# Revit family: Lollygagger Lounge
name_source: partatom
category: Furniture
revit_build: Autodesk Revit 2016 (Build: 20150220_1215(x64)
units: mm (PartAtom-declared; Revit-internal decimal feet)

## family parameters
Always vertical = Yes
Cut with Voids When Loaded = No
OmniClass Number = 23.40.20.00
OmniClass Title = General Furniture and Specialties
Room Calculation Point = No
Shared = No
Work Plane-Based = No

## types (11) — shared parameters
Height Arm = 1' - 6 19/32"
Length = 1' - 10 5/8"
Manufacturer = Loll
Thick = 0' - 0 5/8"
Type Image = lollygagger_lounge_green.jpg
URL = https://lolldesigns.com
Width = 2' - 5 9/32"

## type names (no varying parameters)
- Loll-Black
- Loll-Sunset
- Loll-Chocolate
- Loll-Sky
- Loll-Apple
- Loll-Leaf
- Loll-Evergreen
- Loll-Charcoal
- Loll-Sand
- Loll-Navy Blue
- Loll-White

note: column(s) folded — value = type name in every type: Finish Material

## geometry (parser evidence)
native form markers: Sweep x2
no freeform markers — native parametric forms only
